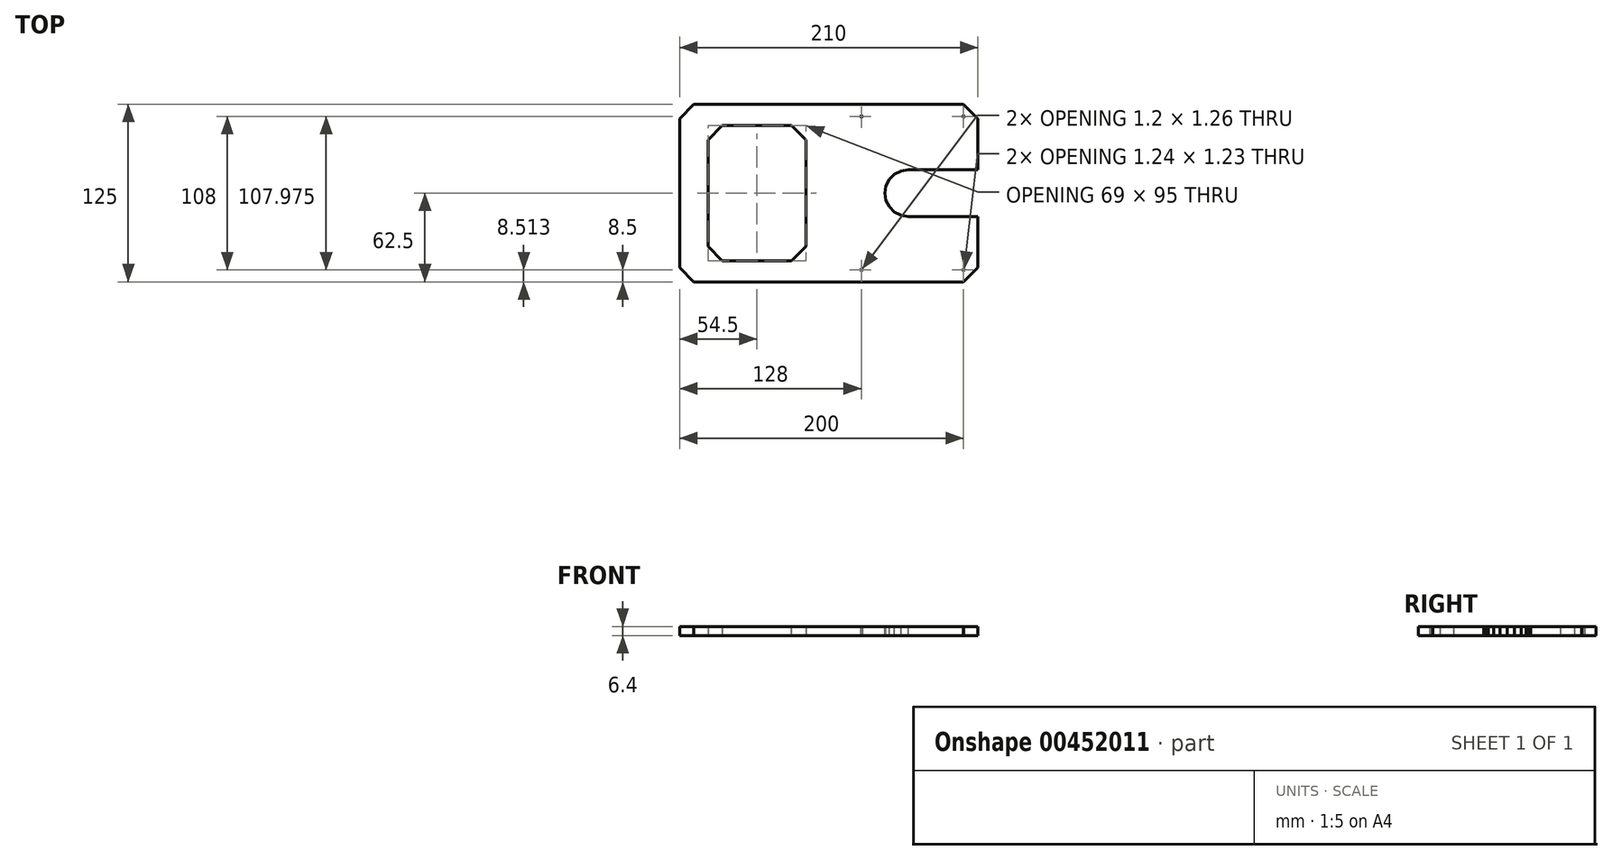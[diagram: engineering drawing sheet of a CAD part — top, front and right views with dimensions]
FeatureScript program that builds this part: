
annotation { "Feature Type Name" : "Feature", "Feature Type Description" : "" }
export const myFeature = defineFeature(function(context is Context, id is Id, definition is map)
    precondition{}
    {
        {
            var Q0;
            Q0=qCreatedBy(makeId("Top.planeOp"),FACE);
            var sketch = newSketch(context, id + "F0", { "sketchPlane" : qUnion([Q0])});
            skLineSegment(sketch, "E0.bottom", {"start": v(105, -62.5) * mm, "end": v(-105, -62.5) * mm});
            skLineSegment(sketch, "E0.top", {"start": v(105, 62.5) * mm, "end": v(-105, 62.5) * mm});
            skLineSegment(sketch, "E0.left", {"start": v(105, -62.5) * mm, "end": v(105, 62.5) * mm});
            skLineSegment(sketch, "E0.right", {"start": v(-105, -62.5) * mm, "end": v(-105, 62.5) * mm});
            skPoint(sketch, "E0.middle", {"position": v(0, 0) * mm});
            skLineSegment(sketch, "E1", {"start": v(-105, 0) * mm, "end": v(105, 0) * mm, "construction": true});
            skLineSegment(sketch, "E2", {"start": v(0, 62.5) * mm, "end": v(0, -62.5) * mm, "construction": true});
            skSolve(sketch);
        }
        {
            var Q0;
            Q0=makeQuery(id+"F0.imprint","IMPRINT",FACE,{"disambiguationData":[TD([[makeQuery(id+"F0.imprint","IMPRINT",EDGE,{"derivedFrom":sQuery(id+"F0.wireOp",EDGE,"E0.bottom")}),-1.0]])]});
            extrude(context, id + "F1", {"entities" : qUnion([Q0]), "depth" : 6.4 * mm});
        }
        {
            var Q0;
            Q0=makeQuery(id+"F1.opExtrude","CAP_FACE",FACE,{"disambiguationData":[OSD([sQuery(id+"F0.wireOp",EDGE,"E0.bottom"),sQuery(id+"F0.wireOp",EDGE,"E0.top"),sQuery(id+"F0.wireOp",EDGE,"E0.left"),sQuery(id+"F0.wireOp",EDGE,"E0.right")])],"isStart":false});
            var sketch = newSketch(context, id + "F2", { "sketchPlane" : qUnion([Q0])});
            skLineSegment(sketch, "E3", {"start": v(56, 16.5) * mm, "end": v(105, 16.5) * mm});
            skLineSegment(sketch, "E4.MirrorCS", {"start": v(56, -16.5) * mm, "end": v(105, -16.5) * mm});
            skLineSegment(sketch, "E5", {"start": v(95, 62.5) * mm, "end": v(95, -62.5) * mm, "construction": true});
            skLineSegment(sketch, "E6", {"start": v(105, 16.5) * mm, "end": v(105, -16.5) * mm});
            skCircle(sketch, "E7.cCircle", {"center": v(56, 0) * mm, "radius": 16.5 * mm, "construction": true});
            skLineSegment(sketch, "E7.0", {"start": v(56, 16.5) * mm, "end": v(61.1, 15.7) * mm, "construction": true});
            skLineSegment(sketch, "E7.1", {"start": v(61.1, 15.7) * mm, "end": v(65.7, 13.35) * mm, "construction": true});
            skLineSegment(sketch, "E7.2", {"start": v(65.7, 13.35) * mm, "end": v(69.35, 9.7) * mm, "construction": true});
            skLineSegment(sketch, "E7.3", {"start": v(69.35, 9.7) * mm, "end": v(71.7, 5.1) * mm, "construction": true});
            skLineSegment(sketch, "E7.4", {"start": v(71.7, 5.1) * mm, "end": v(72.5, 0) * mm, "construction": true});
            skLineSegment(sketch, "E7.5", {"start": v(72.5, 0) * mm, "end": v(71.7, -5.1) * mm, "construction": true});
            skLineSegment(sketch, "E7.6", {"start": v(71.7, -5.1) * mm, "end": v(69.35, -9.7) * mm, "construction": true});
            skLineSegment(sketch, "E7.7", {"start": v(69.35, -9.7) * mm, "end": v(65.7, -13.35) * mm, "construction": true});
            skLineSegment(sketch, "E7.8", {"start": v(65.7, -13.35) * mm, "end": v(61.1, -15.7) * mm, "construction": true});
            skLineSegment(sketch, "E7.9", {"start": v(61.1, -15.7) * mm, "end": v(56, -16.5) * mm, "construction": true});
            skLineSegment(sketch, "E7.10", {"start": v(56, -16.5) * mm, "end": v(50.9, -15.7) * mm});
            skLineSegment(sketch, "E7.11", {"start": v(50.9, -15.7) * mm, "end": v(46.3, -13.35) * mm});
            skLineSegment(sketch, "E7.12", {"start": v(46.3, -13.35) * mm, "end": v(42.65, -9.7) * mm});
            skLineSegment(sketch, "E7.13", {"start": v(42.65, -9.7) * mm, "end": v(40.3, -5.1) * mm});
            skLineSegment(sketch, "E7.14", {"start": v(40.3, -5.1) * mm, "end": v(39.5, 0) * mm});
            skLineSegment(sketch, "E7.15", {"start": v(39.5, 0) * mm, "end": v(40.3, 5.1) * mm});
            skLineSegment(sketch, "E7.16", {"start": v(40.3, 5.1) * mm, "end": v(42.65, 9.7) * mm});
            skLineSegment(sketch, "E7.17", {"start": v(42.65, 9.7) * mm, "end": v(46.3, 13.35) * mm});
            skLineSegment(sketch, "E7.18", {"start": v(46.3, 13.35) * mm, "end": v(50.9, 15.7) * mm});
            skLineSegment(sketch, "E7.19", {"start": v(50.9, 15.7) * mm, "end": v(56, 16.5) * mm});
            skSolve(sketch);
        }
        {
            var Q0;
            Q0=qSketchRegion(id+"F2",true);
            extrude(context, id + "F3", {"entities" : qUnion([Q0]), "operationType" : NewBodyOperationType.REMOVE, "oppositeDirection" : true, "depth" : 25 * mm});
        }
        {
            var Q0;
            Q0=qCreatedBy(makeId("Top.planeOp"),FACE);
            var sketch = newSketch(context, id + "F4", { "sketchPlane" : qUnion([Q0])});
            skLineSegment(sketch, "E8.0", {"start": v(95, 62.5) * mm, "end": v(95, -62.5) * mm, "construction": true});
            skLineSegment(sketch, "E9", {"start": v(0, 0) * mm, "end": v(95, 0) * mm, "construction": true});
            skCircle(sketch, "E10.cCircle", {"center": v(95, 54) * mm, "radius": 0.6 * mm, "construction": true});
            skLineSegment(sketch, "E10.0", {"start": v(95, 53.37) * mm, "end": v(94.66, 53.47) * mm});
            skLineSegment(sketch, "E10.1", {"start": v(94.66, 53.47) * mm, "end": v(94.43, 53.74) * mm});
            skLineSegment(sketch, "E10.2", {"start": v(94.43, 53.74) * mm, "end": v(94.38, 54.09) * mm});
            skLineSegment(sketch, "E10.3", {"start": v(94.38, 54.09) * mm, "end": v(94.53, 54.4) * mm});
            skLineSegment(sketch, "E10.4", {"start": v(94.53, 54.4) * mm, "end": v(94.82, 54.6) * mm});
            skLineSegment(sketch, "E10.5", {"start": v(94.82, 54.6) * mm, "end": v(95.18, 54.6) * mm});
            skLineSegment(sketch, "E10.6", {"start": v(95.18, 54.6) * mm, "end": v(95.47, 54.4) * mm});
            skLineSegment(sketch, "E10.7", {"start": v(95.47, 54.4) * mm, "end": v(95.62, 54.09) * mm});
            skLineSegment(sketch, "E10.8", {"start": v(95.62, 54.09) * mm, "end": v(95.57, 53.74) * mm});
            skLineSegment(sketch, "E10.9", {"start": v(95.57, 53.74) * mm, "end": v(95.34, 53.47) * mm});
            skLineSegment(sketch, "E10.10", {"start": v(95.34, 53.47) * mm, "end": v(95, 53.37) * mm});
            skPoint(sketch, "E10.0.midPoint", {"position": v(94.83, 53.42) * mm});
            skCircle(sketch, "E11.MirrorC", {"center": v(95, -54) * mm, "radius": 0.6 * mm, "construction": true});
            skLineSegment(sketch, "E12.MirrorCS", {"start": v(95.62, -54.09) * mm, "end": v(95.57, -53.74) * mm});
            skLineSegment(sketch, "E13.MirrorCS", {"start": v(95.47, -54.4) * mm, "end": v(95.62, -54.09) * mm});
            skLineSegment(sketch, "E14.MirrorCS", {"start": v(95.18, -54.6) * mm, "end": v(95.47, -54.4) * mm});
            skLineSegment(sketch, "E15.MirrorCS", {"start": v(94.82, -54.6) * mm, "end": v(95.18, -54.6) * mm});
            skLineSegment(sketch, "E16.MirrorCS", {"start": v(94.53, -54.4) * mm, "end": v(94.82, -54.6) * mm});
            skLineSegment(sketch, "E17.MirrorCS", {"start": v(94.38, -54.09) * mm, "end": v(94.53, -54.4) * mm});
            skLineSegment(sketch, "E18.MirrorCS", {"start": v(94.43, -53.74) * mm, "end": v(94.38, -54.09) * mm});
            skLineSegment(sketch, "E19.MirrorCS", {"start": v(94.66, -53.47) * mm, "end": v(94.43, -53.74) * mm});
            skLineSegment(sketch, "E20.MirrorCS", {"start": v(95, -53.37) * mm, "end": v(94.66, -53.47) * mm});
            skLineSegment(sketch, "E21.MirrorCS", {"start": v(95.57, -53.74) * mm, "end": v(95.34, -53.47) * mm});
            skLineSegment(sketch, "E22.MirrorCS", {"start": v(95.34, -53.47) * mm, "end": v(95, -53.37) * mm});
            skPoint(sketch, "E23.MirrorP", {"position": v(94.83, -53.42) * mm});
            skLineSegment(sketch, "E24", {"start": v(23, 62.5) * mm, "end": v(23, -62.5) * mm, "construction": true});
            skCircle(sketch, "E25.cCircle", {"center": v(23, 54) * mm, "radius": 0.6 * mm, "construction": true});
            skLineSegment(sketch, "E25.0", {"start": v(23.6, 53.8) * mm, "end": v(23.37, 53.49) * mm});
            skLineSegment(sketch, "E25.1", {"start": v(23.37, 53.49) * mm, "end": v(23, 53.37) * mm});
            skLineSegment(sketch, "E25.2", {"start": v(23, 53.37) * mm, "end": v(22.63, 53.49) * mm});
            skLineSegment(sketch, "E25.3", {"start": v(22.63, 53.49) * mm, "end": v(22.4, 53.8) * mm});
            skLineSegment(sketch, "E25.4", {"start": v(22.4, 53.8) * mm, "end": v(22.4, 54.2) * mm});
            skLineSegment(sketch, "E25.5", {"start": v(22.4, 54.2) * mm, "end": v(22.63, 54.51) * mm});
            skLineSegment(sketch, "E25.6", {"start": v(22.63, 54.51) * mm, "end": v(23, 54.63) * mm});
            skLineSegment(sketch, "E25.7", {"start": v(23, 54.63) * mm, "end": v(23.37, 54.51) * mm});
            skLineSegment(sketch, "E25.8", {"start": v(23.37, 54.51) * mm, "end": v(23.6, 54.2) * mm});
            skLineSegment(sketch, "E25.9", {"start": v(23.6, 54.2) * mm, "end": v(23.6, 53.8) * mm});
            skPoint(sketch, "E25.0.midPoint", {"position": v(23.49, 53.65) * mm});
            skLineSegment(sketch, "E26.MirrorCS", {"start": v(22.4, -53.8) * mm, "end": v(22.4, -54.2) * mm});
            skLineSegment(sketch, "E27.MirrorCS", {"start": v(23.37, -53.49) * mm, "end": v(23, -53.37) * mm});
            skLineSegment(sketch, "E28.MirrorCS", {"start": v(23, -54.63) * mm, "end": v(23.37, -54.51) * mm});
            skLineSegment(sketch, "E29.MirrorCS", {"start": v(23.6, -53.8) * mm, "end": v(23.37, -53.49) * mm});
            skLineSegment(sketch, "E30.MirrorCS", {"start": v(23.6, -54.2) * mm, "end": v(23.6, -53.8) * mm});
            skLineSegment(sketch, "E31.MirrorCS", {"start": v(22.4, -54.2) * mm, "end": v(22.63, -54.51) * mm});
            skLineSegment(sketch, "E32.MirrorCS", {"start": v(22.63, -54.51) * mm, "end": v(23, -54.63) * mm});
            skLineSegment(sketch, "E33.MirrorCS", {"start": v(22.63, -53.49) * mm, "end": v(22.4, -53.8) * mm});
            skLineSegment(sketch, "E34.MirrorCS", {"start": v(23, -53.37) * mm, "end": v(22.63, -53.49) * mm});
            skLineSegment(sketch, "E35.MirrorCS", {"start": v(23.37, -54.51) * mm, "end": v(23.6, -54.2) * mm});
            skCircle(sketch, "E36.MirrorC", {"center": v(23, -54) * mm, "radius": 0.6 * mm, "construction": true});
            skPoint(sketch, "E37.MirrorP", {"position": v(23.49, -53.65) * mm});
            skSolve(sketch);
        }
        {
            var Q0;
            Q0=qSketchRegion(id+"F4",true);
            extrude(context, id + "F5", {"entities" : qUnion([Q0]), "operationType" : NewBodyOperationType.REMOVE, "endBound" : BoundingType.UP_TO_NEXT, "depth" : 25 * mm});
        }
        {
            var Q0;
            Q0=makeQuery(id+"F1.opExtrude","SWEPT_EDGE",EDGE,{"disambiguationData":[OSD([sQuery(id+"F0.wireOp",EDGE,"E0.top"),sQuery(id+"F0.wireOp",EDGE,"E0.right")])]});
            var Q1;
            Q1=makeQuery(id+"F1.opExtrude","SWEPT_EDGE",EDGE,{"disambiguationData":[OSD([sQuery(id+"F0.wireOp",EDGE,"E0.top"),sQuery(id+"F0.wireOp",EDGE,"E0.left")])]});
            var Q2;
            Q2=makeQuery(id+"F1.opExtrude","SWEPT_EDGE",EDGE,{"disambiguationData":[OSD([sQuery(id+"F0.wireOp",EDGE,"E0.bottom"),sQuery(id+"F0.wireOp",EDGE,"E0.left")])]});
            var Q3;
            Q3=makeQuery(id+"F1.opExtrude","SWEPT_EDGE",EDGE,{"disambiguationData":[OSD([sQuery(id+"F0.wireOp",EDGE,"E0.bottom"),sQuery(id+"F0.wireOp",EDGE,"E0.right")])]});
            chamfer(context, id + "F6", {"entities" : qUnion([Q0, Q1, Q2, Q3]), "width" : 10 * mm, "tangentPropagation" : true});
        }
        {
            var Q0;
            Q0=makeQuery(id+"F1.opExtrude","CAP_FACE",FACE,{"disambiguationData":[OSD([sQuery(id+"F0.wireOp",EDGE,"E0.bottom"),sQuery(id+"F0.wireOp",EDGE,"E0.top"),sQuery(id+"F0.wireOp",EDGE,"E0.left"),sQuery(id+"F0.wireOp",EDGE,"E0.right")])],"isStart":true});
            var sketch = newSketch(context, id + "F7", { "sketchPlane" : qUnion([Q0])});
            skLineSegment(sketch, "E38.bottom", {"start": v(-16, -47.5) * mm, "end": v(-85, -47.5) * mm});
            skLineSegment(sketch, "E38.top", {"start": v(-16, 47.5) * mm, "end": v(-85, 47.5) * mm});
            skLineSegment(sketch, "E38.left", {"start": v(-16, -47.5) * mm, "end": v(-16, 47.5) * mm});
            skLineSegment(sketch, "E38.right", {"start": v(-85, -47.5) * mm, "end": v(-85, 47.5) * mm});
            skPoint(sketch, "E38.middle", {"position": v(-50.5, 0) * mm});
            skSolve(sketch);
        }
        {
            var Q0;
            Q0=makeQuery(id+"F7.imprint","IMPRINT",FACE,{"disambiguationData":[TD([[makeQuery(id+"F7.imprint","IMPRINT",EDGE,{"derivedFrom":sQuery(id+"F7.wireOp",EDGE,"E38.bottom")}),-1.0]])]});
            extrude(context, id + "F8", {"entities" : qUnion([Q0]), "operationType" : NewBodyOperationType.REMOVE, "endBound" : BoundingType.THROUGH_ALL, "oppositeDirection" : true, "depth" : 25 * mm});
        }
        {
            var Q0;
            Q0=makeQuery(id+"F8.boolean.opBoolean","COPY",EDGE,{"derivedFrom":makeQuery(id+"F8.opExtrude","SWEPT_EDGE",EDGE,{"disambiguationData":[OSD([sQuery(id+"F7.wireOp",EDGE,"E38.bottom"),sQuery(id+"F7.wireOp",EDGE,"E38.right")])]})});
            var Q1;
            Q1=makeQuery(id+"F8.boolean.opBoolean","COPY",EDGE,{"derivedFrom":makeQuery(id+"F8.opExtrude","SWEPT_EDGE",EDGE,{"disambiguationData":[OSD([sQuery(id+"F7.wireOp",EDGE,"E38.bottom"),sQuery(id+"F7.wireOp",EDGE,"E38.left")])]})});
            var Q2;
            Q2=makeQuery(id+"F8.boolean.opBoolean","COPY",EDGE,{"derivedFrom":makeQuery(id+"F8.opExtrude","SWEPT_EDGE",EDGE,{"disambiguationData":[OSD([sQuery(id+"F7.wireOp",EDGE,"E38.top"),sQuery(id+"F7.wireOp",EDGE,"E38.left")])]})});
            var Q3;
            Q3=makeQuery(id+"F8.boolean.opBoolean","COPY",EDGE,{"derivedFrom":makeQuery(id+"F8.opExtrude","SWEPT_EDGE",EDGE,{"disambiguationData":[OSD([sQuery(id+"F7.wireOp",EDGE,"E38.top"),sQuery(id+"F7.wireOp",EDGE,"E38.right")])]})});
            chamfer(context, id + "F9", {"entities" : qUnion([Q0, Q1, Q2, Q3]), "width" : 10 * mm, "tangentPropagation" : true});
        }
    });
